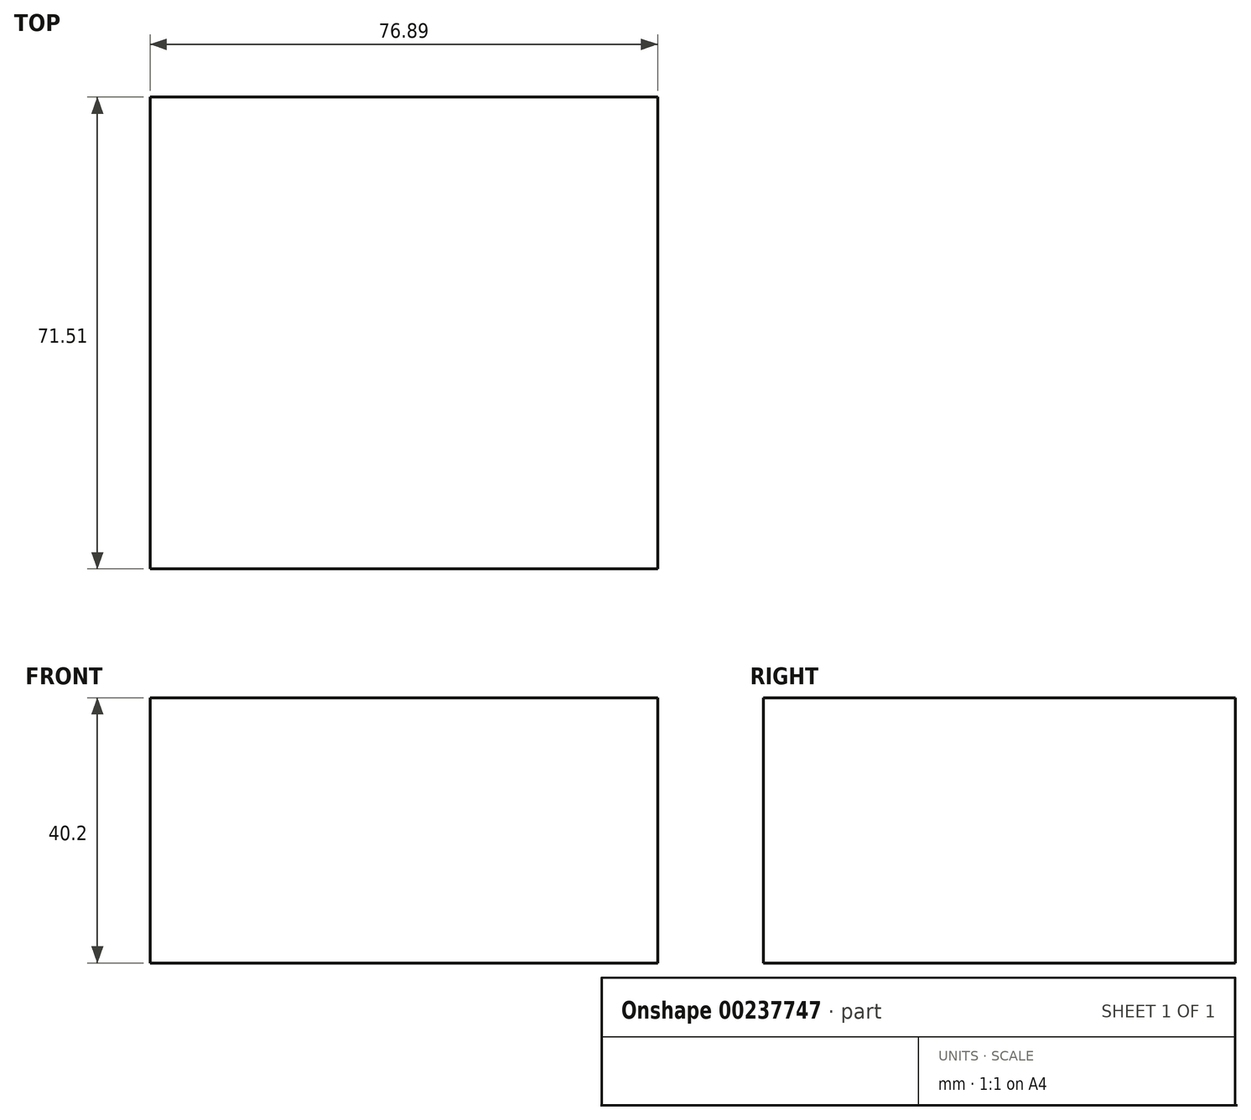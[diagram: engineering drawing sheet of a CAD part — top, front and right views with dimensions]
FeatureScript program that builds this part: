
annotation { "Feature Type Name" : "Feature", "Feature Type Description" : "" }
export const myFeature = defineFeature(function(context is Context, id is Id, definition is map)
    precondition{}
    {
        {
            var Q0;
            Q0=qCreatedBy(makeId("Top.planeOp"),FACE);
            var sketch = newSketch(context, id + "F0", { "sketchPlane" : qUnion([Q0])});
            skLineSegment(sketch, "E0.bottom", {"start": v(-233.78, -93.2) * mm, "end": v(-156.89, -93.2) * mm});
            skLineSegment(sketch, "E0.top", {"start": v(-233.78, -21.7) * mm, "end": v(-156.89, -21.7) * mm});
            skLineSegment(sketch, "E0.left", {"start": v(-233.78, -93.2) * mm, "end": v(-233.78, -21.7) * mm});
            skLineSegment(sketch, "E0.right", {"start": v(-156.89, -93.2) * mm, "end": v(-156.89, -21.7) * mm});
            skSolve(sketch);
        }
        {
            var Q0;
            Q0=sQuery(id+"F0.wireOp",EDGE,"E0.left");
            var Q1;
            Q1=sQuery(id+"F0.wireOp",EDGE,"E0.bottom");
            var Q2;
            Q2=sQuery(id+"F0.wireOp",EDGE,"E0.right");
            var Q3;
            Q3=sQuery(id+"F0.wireOp",EDGE,"E0.top");
            extrude(context, id + "F1", {"bodyType" : ToolBodyType.SURFACE, "surfaceEntities" : qUnion([Q0, Q1, Q2, Q3]), "depth" : 40.2 * mm});
        }
    });
